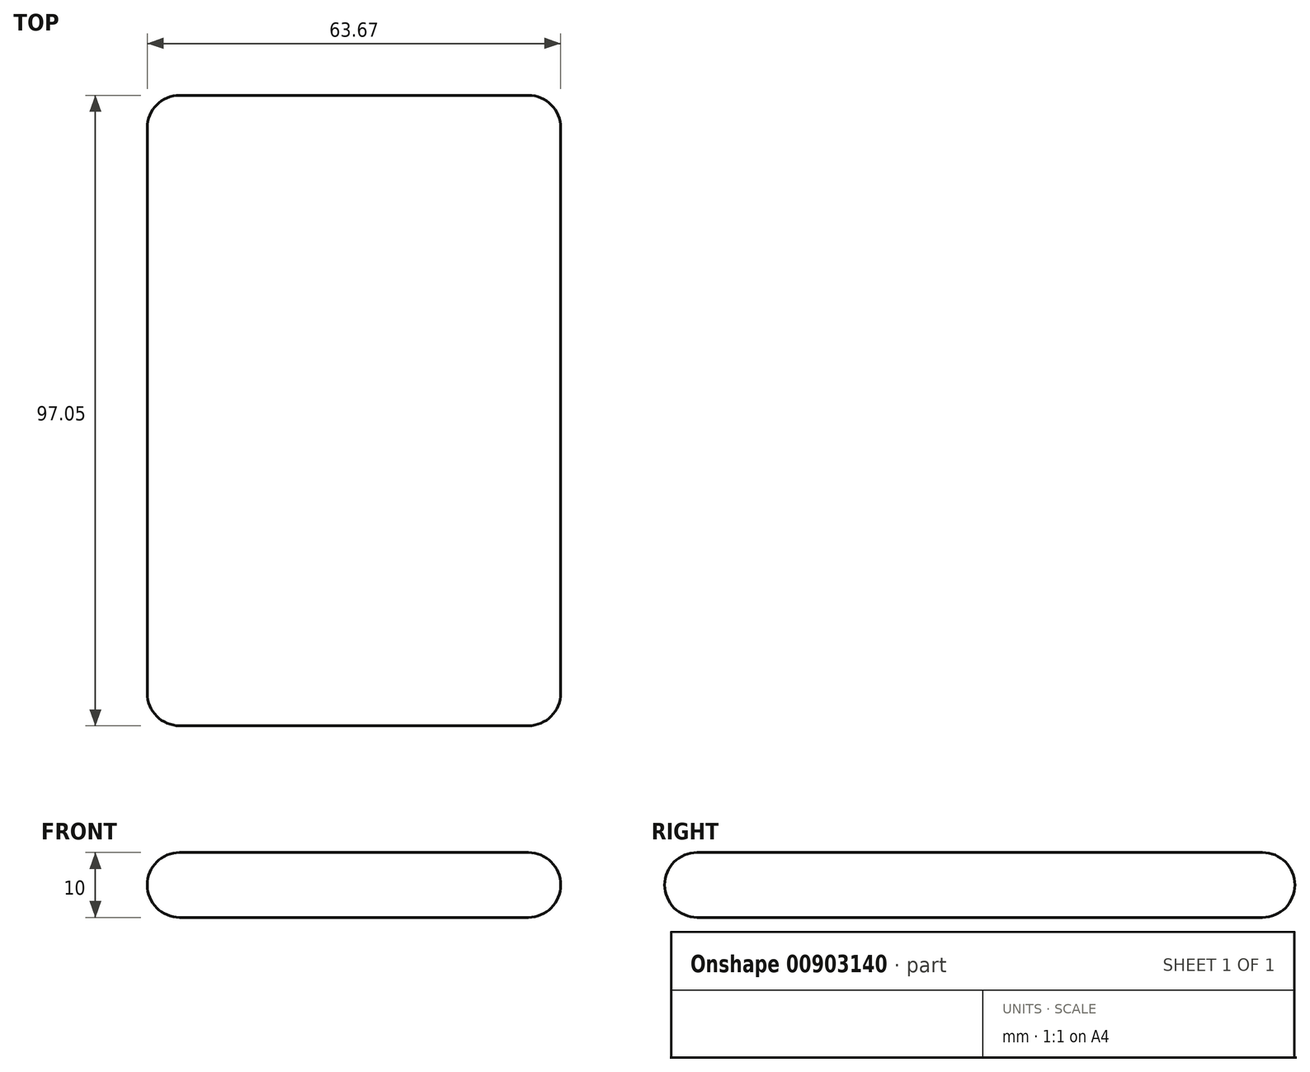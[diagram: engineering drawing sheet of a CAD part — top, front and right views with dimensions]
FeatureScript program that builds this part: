
annotation { "Feature Type Name" : "Feature", "Feature Type Description" : "" }
export const myFeature = defineFeature(function(context is Context, id is Id, definition is map)
    precondition{}
    {
        {
            var Q0;
            Q0=qCreatedBy(makeId("Top.planeOp"),FACE);
            var sketch = newSketch(context, id + "F0", { "sketchPlane" : qUnion([Q0])});
            skLineSegment(sketch, "E0.bottom", {"start": v(-43.13, 40.2) * mm, "end": v(20.54, 40.2) * mm});
            skLineSegment(sketch, "E0.top", {"start": v(-43.13, -56.84) * mm, "end": v(20.54, -56.84) * mm});
            skLineSegment(sketch, "E0.left", {"start": v(-43.13, 40.2) * mm, "end": v(-43.13, -56.84) * mm});
            skLineSegment(sketch, "E0.right", {"start": v(20.54, 40.2) * mm, "end": v(20.54, -56.84) * mm});
            skSolve(sketch);
        }
        {
            var Q0;
            Q0 = qSketchRegion(id + "F0", true);
            extrude(context, id + "F1", {"entities" : qUnion([Q0]), "depth" : 10 * mm, "offsetDistance" : 25 * mm});
        }
        {
            var Q0;
            Q0=makeQuery(id+"F1.opExtrude","SWEPT_FACE",FACE,{"disambiguationData":[OSD([sQuery(id+"F0.wireOp",EDGE,"E0.right")])]});
            var Q1;
            Q1=makeQuery(id+"F1.opExtrude","SWEPT_FACE",FACE,{"disambiguationData":[OSD([sQuery(id+"F0.wireOp",EDGE,"E0.bottom")])]});
            var Q2;
            Q2=makeQuery(id+"F1.opExtrude","SWEPT_FACE",FACE,{"disambiguationData":[OSD([sQuery(id+"F0.wireOp",EDGE,"E0.left")])]});
            var Q3;
            Q3=makeQuery(id+"F1.opExtrude","SWEPT_FACE",FACE,{"disambiguationData":[OSD([sQuery(id+"F0.wireOp",EDGE,"E0.top")])]});
            fillet(context, id + "F2", {"entities" : qUnion([Q0, Q1, Q2, Q3]), "radius" : 5 * mm, "tangentPropagation" : true, "allowEdgeOverflow" : false});
        }
    });
